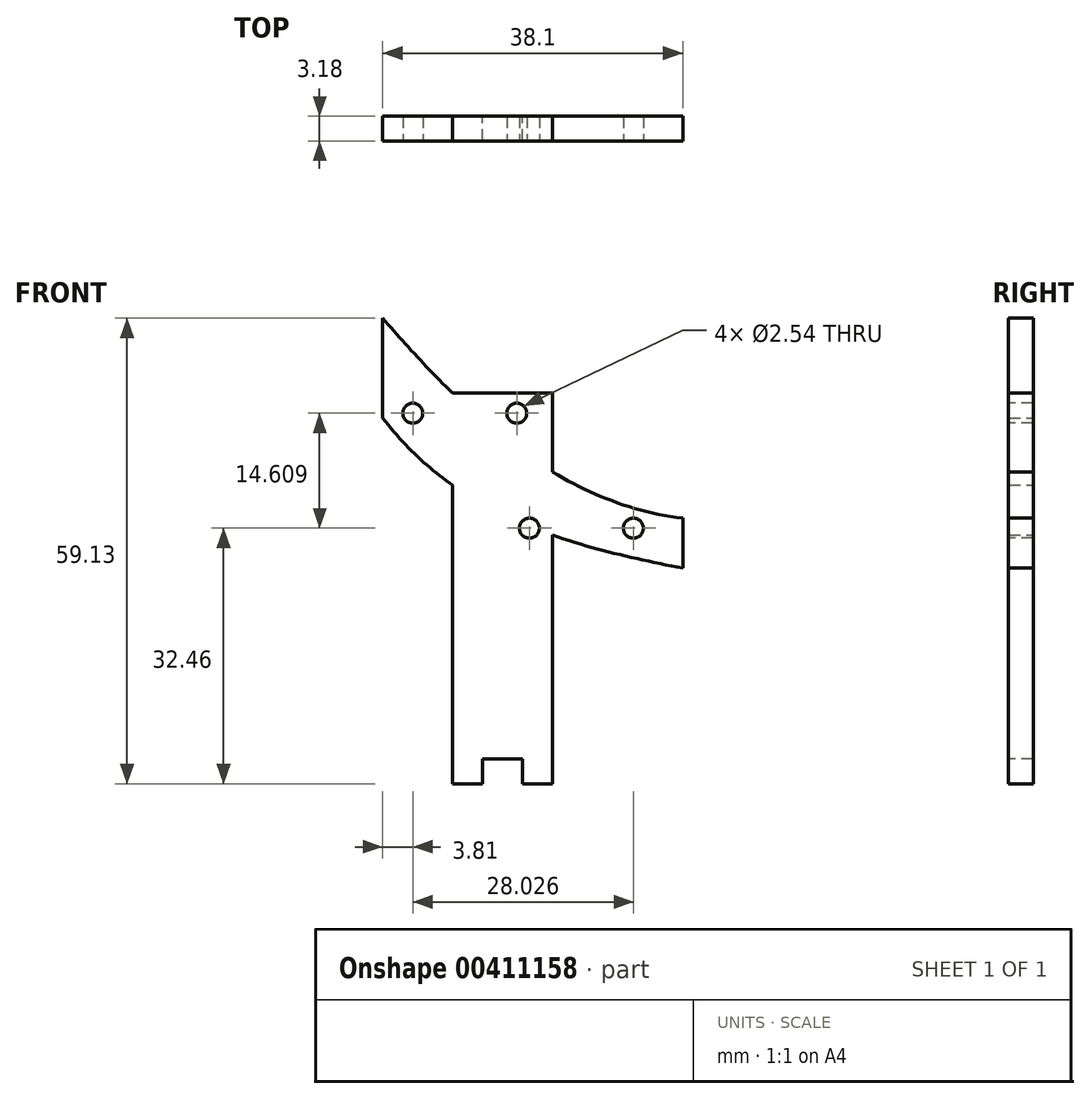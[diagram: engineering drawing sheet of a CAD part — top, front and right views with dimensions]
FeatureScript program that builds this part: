
annotation { "Feature Type Name" : "Feature", "Feature Type Description" : "" }
export const myFeature = defineFeature(function(context is Context, id is Id, definition is map)
    precondition{}
    {
        {
            var Q0;
            Q0=qCreatedBy(makeId("Front.planeOp"),FACE);
            var sketch = newSketch(context, id + "F0", { "sketchPlane" : qUnion([Q0])});
            skLineSegment(sketch, "E0", {"start": v(0, 0) * mm, "end": v(0, 6.35) * mm});
            skLineSegment(sketch, "E1", {"start": v(-38.1, 31.75) * mm, "end": v(-38.1, 19.05) * mm});
            skFitSpline(sketch, "E2", {"points": [v(-38.1, 19.05) * mm, v(0, 0) * mm], "startDerivative": vector(29.18, -37.97) * mm, "endDerivative": vector(42.34, -8.3) * mm});
            skFitSpline(sketch, "E3", {"points": [v(-38.1, 31.75) * mm, v(0, 6.35) * mm], "startDerivative": vector(26.62, -30.7) * mm, "endDerivative": vector(50, -5.86) * mm});
            skSolve(sketch);
        }
        {
            var Q0;
            Q0 = qSketchRegion(id + "F0", true);
            extrude(context, id + "F1", {"entities" : qUnion([Q0]), "depth" : 3.17 * mm});
        }
        {
            var Q0;
            Q0=makeQuery(id+"F1.opExtrude","CAP_FACE",FACE,{"disambiguationData":[OSD([sQuery(id+"F0.wireOp",EDGE,"E0"),sQuery(id+"F0.wireOp",EDGE,"E1"),sQuery(id+"F0.wireOp",EDGE,"E2"),sQuery(id+"F0.wireOp",EDGE,"E3")])],"isStart":false});
            var sketch = newSketch(context, id + "F2", { "sketchPlane" : qUnion([Q0])});
            skLineSegment(sketch, "E4.bottom", {"start": v(-29.22, 12.23) * mm, "end": v(-16.52, 12.23) * mm});
            skLineSegment(sketch, "E4.top", {"start": v(-29.22, -27.38) * mm, "end": v(-16.52, -27.38) * mm});
            skLineSegment(sketch, "E4.left", {"start": v(-29.22, 12.23) * mm, "end": v(-29.22, -27.38) * mm});
            skLineSegment(sketch, "E4.right", {"start": v(-16.52, 12.23) * mm, "end": v(-16.52, -27.38) * mm});
            skSolve(sketch);
        }
        {
            var Q0;
            Q0 = qSketchRegion(id + "F2", true);
            var Q1;
            Q1=makeQuery(id+"F1.opExtrude","CAP_FACE",FACE,{"disambiguationData":[OSD([sQuery(id+"F0.wireOp",EDGE,"E0"),sQuery(id+"F0.wireOp",EDGE,"E1"),sQuery(id+"F0.wireOp",EDGE,"E2"),sQuery(id+"F0.wireOp",EDGE,"E3")])],"isStart":true});
            extrude(context, id + "F3", {"entities" : qUnion([Q0]), "operationType" : NewBodyOperationType.ADD, "endBound" : BoundingType.UP_TO_SURFACE, "oppositeDirection" : true, "endBoundEntityFace" : qUnion([Q1]), "depth" : 25.4 * mm});
        }
        {
            var Q0;
            Q0=makeQuery(id+"F3.boolean.opBoolean","MERGE",FACE,{"derivedFrom":[makeQuery(id+"F1.opExtrude","CAP_FACE",FACE,{"disambiguationData":[OSD([sQuery(id+"F0.wireOp",EDGE,"E0"),sQuery(id+"F0.wireOp",EDGE,"E1"),sQuery(id+"F0.wireOp",EDGE,"E2"),sQuery(id+"F0.wireOp",EDGE,"E3")])],"isStart":false}),makeQuery(id+"F3.opExtrude","CAP_FACE",FACE,{"disambiguationData":[OSD([sQuery(id+"F2.wireOp",EDGE,"E4.bottom"),sQuery(id+"F2.wireOp",EDGE,"E4.top"),sQuery(id+"F2.wireOp",EDGE,"E4.left"),sQuery(id+"F2.wireOp",EDGE,"E4.right")])],"isStart":true})]});
            var sketch = newSketch(context, id + "F4", { "sketchPlane" : qUnion([Q0])});
            skLineSegment(sketch, "E5.bottom", {"start": v(-29.22, 10.54) * mm, "end": v(-16.52, 10.54) * mm});
            skLineSegment(sketch, "E5.top", {"start": v(-29.22, 22.23) * mm, "end": v(-16.52, 22.23) * mm});
            skLineSegment(sketch, "E5.left", {"start": v(-29.22, 10.54) * mm, "end": v(-29.22, 22.23) * mm});
            skLineSegment(sketch, "E5.right", {"start": v(-16.52, 10.54) * mm, "end": v(-16.52, 22.23) * mm});
            skSolve(sketch);
        }
        {
            var Q0;
            {var subQ0=sQuery(id+"F4.wireOp",EDGE,"E5.top");Q0=makeQuery(id+"F4.imprint","IMPRINT",FACE,{"disambiguationData":[TD([[makeQuery(id+"F4.imprint","IMPRINT",EDGE,{"derivedFrom":subQ0}),-1.0]])]});}
            var Q1;
            {var subQ0=sQuery(id+"F0.wireOp",EDGE,"E3");var subQ1=sQuery(id+"F0.wireOp",EDGE,"E2");var subQ2=sQuery(id+"F0.wireOp",EDGE,"E1");var subQ3=sQuery(id+"F0.wireOp",EDGE,"E0");Q1=makeQuery(id+"F3.boolean.opBoolean","MERGE",FACE,{"derivedFrom":[makeQuery(id+"F1.opExtrude","CAP_FACE",FACE,{"disambiguationData":[OSD([subQ3,subQ2,subQ1,subQ0])],"isStart":true}),makeQuery(id+"F3.opExtrude","CAP_FACE",FACE,{"disambiguationData":[OSD([subQ3,subQ2,subQ1,subQ0])],"isStart":false})]});}
            extrude(context, id + "F5", {"entities" : qUnion([Q0]), "operationType" : NewBodyOperationType.ADD, "endBound" : BoundingType.UP_TO_SURFACE, "oppositeDirection" : true, "endBoundEntityFace" : qUnion([Q1]), "depth" : 25.4 * mm});
        }
        {
            var Q0;
            {var subQ0=sQuery(id+"F0.wireOp",EDGE,"E3");Q0=makeQuery(id+"F5.boolean.opBoolean","MERGE",FACE,{"derivedFrom":[makeQuery(id+"F3.boolean.opBoolean","MERGE",FACE,{"derivedFrom":[makeQuery(id+"F1.opExtrude","CAP_FACE",FACE,{"disambiguationData":[OSD([sQuery(id+"F0.wireOp",EDGE,"E0"),sQuery(id+"F0.wireOp",EDGE,"E1"),sQuery(id+"F0.wireOp",EDGE,"E2"),subQ0])],"isStart":false}),makeQuery(id+"F3.opExtrude","CAP_FACE",FACE,{"disambiguationData":[OSD([sQuery(id+"F2.wireOp",EDGE,"E4.bottom"),sQuery(id+"F2.wireOp",EDGE,"E4.top"),sQuery(id+"F2.wireOp",EDGE,"E4.left"),sQuery(id+"F2.wireOp",EDGE,"E4.right")])],"isStart":true})]}),makeQuery(id+"F5.opExtrude","CAP_FACE",FACE,{"disambiguationData":[OSD([subQ0,sQuery(id+"F4.wireOp",EDGE,"E5.top"),sQuery(id+"F4.wireOp",EDGE,"E5.right")])],"isStart":true})]});}
            var sketch = newSketch(context, id + "F6", { "sketchPlane" : qUnion([Q0])});
            skCircle(sketch, "E6", {"center": v(-34.3, 19.69) * mm, "radius": 1.27 * mm});
            skCircle(sketch, "E7", {"center": v(-21.08, 19.69) * mm, "radius": 1.27 * mm});
            skSolve(sketch);
        }
        {
            var Q0;
            Q0 = qSketchRegion(id + "F6", true);
            extrude(context, id + "F7", {"entities" : qUnion([Q0]), "operationType" : NewBodyOperationType.REMOVE, "endBound" : BoundingType.THROUGH_ALL, "oppositeDirection" : true, "depth" : 25.4 * mm});
        }
        {
            var Q0;
            {var subQ0=sQuery(id+"F0.wireOp",EDGE,"E3");Q0=makeQuery(id+"F5.boolean.opBoolean","MERGE",FACE,{"derivedFrom":[makeQuery(id+"F3.boolean.opBoolean","MERGE",FACE,{"derivedFrom":[makeQuery(id+"F1.opExtrude","CAP_FACE",FACE,{"disambiguationData":[OSD([sQuery(id+"F0.wireOp",EDGE,"E0"),sQuery(id+"F0.wireOp",EDGE,"E1"),sQuery(id+"F0.wireOp",EDGE,"E2"),subQ0])],"isStart":false}),makeQuery(id+"F3.opExtrude","CAP_FACE",FACE,{"disambiguationData":[OSD([sQuery(id+"F2.wireOp",EDGE,"E4.bottom"),sQuery(id+"F2.wireOp",EDGE,"E4.top"),sQuery(id+"F2.wireOp",EDGE,"E4.left"),sQuery(id+"F2.wireOp",EDGE,"E4.right")])],"isStart":true})]}),makeQuery(id+"F5.opExtrude","CAP_FACE",FACE,{"disambiguationData":[OSD([subQ0,sQuery(id+"F4.wireOp",EDGE,"E5.top"),sQuery(id+"F4.wireOp",EDGE,"E5.right")])],"isStart":true})]});}
            var sketch = newSketch(context, id + "F8", { "sketchPlane" : qUnion([Q0])});
            skCircle(sketch, "E8", {"center": v(-6.26, 5.08) * mm, "radius": 1.27 * mm});
            skCircle(sketch, "E9", {"center": v(-19.47, 5.08) * mm, "radius": 1.27 * mm});
            skSolve(sketch);
        }
        {
            var Q0;
            Q0=makeQuery(id+"F8.imprint","IMPRINT",FACE,{"disambiguationData":[TD([[makeQuery(id+"F8.imprint","IMPRINT",EDGE,{"derivedFrom":sQuery(id+"F8.wireOp",EDGE,"E9")}),1.0]])]});
            var Q1;
            Q1=makeQuery(id+"F8.imprint","IMPRINT",FACE,{"disambiguationData":[TD([[makeQuery(id+"F8.imprint","IMPRINT",EDGE,{"derivedFrom":sQuery(id+"F8.wireOp",EDGE,"E8")}),1.0]])]});
            extrude(context, id + "F9", {"entities" : qUnion([Q0, Q1]), "operationType" : NewBodyOperationType.REMOVE, "endBound" : BoundingType.THROUGH_ALL, "oppositeDirection" : true, "depth" : 25.4 * mm});
        }
        {
            var Q0;
            {var subQ0=sQuery(id+"F0.wireOp",EDGE,"E3");Q0=makeQuery(id+"F5.boolean.opBoolean","MERGE",FACE,{"derivedFrom":[makeQuery(id+"F3.boolean.opBoolean","MERGE",FACE,{"derivedFrom":[makeQuery(id+"F1.opExtrude","CAP_FACE",FACE,{"disambiguationData":[OSD([sQuery(id+"F0.wireOp",EDGE,"E0"),sQuery(id+"F0.wireOp",EDGE,"E1"),sQuery(id+"F0.wireOp",EDGE,"E2"),subQ0])],"isStart":false}),makeQuery(id+"F3.opExtrude","CAP_FACE",FACE,{"disambiguationData":[OSD([sQuery(id+"F2.wireOp",EDGE,"E4.bottom"),sQuery(id+"F2.wireOp",EDGE,"E4.top"),sQuery(id+"F2.wireOp",EDGE,"E4.left"),sQuery(id+"F2.wireOp",EDGE,"E4.right")])],"isStart":true})]}),makeQuery(id+"F5.opExtrude","CAP_FACE",FACE,{"disambiguationData":[OSD([subQ0,sQuery(id+"F4.wireOp",EDGE,"E5.top"),sQuery(id+"F4.wireOp",EDGE,"E5.right")])],"isStart":true})]});}
            var sketch = newSketch(context, id + "F10", { "sketchPlane" : qUnion([Q0])});
            skLineSegment(sketch, "E10.bottom", {"start": v(-25.41, -24.2) * mm, "end": v(-20.33, -24.2) * mm});
            skLineSegment(sketch, "E10.top", {"start": v(-25.41, -30.56) * mm, "end": v(-20.33, -30.56) * mm});
            skLineSegment(sketch, "E10.left", {"start": v(-25.41, -24.2) * mm, "end": v(-25.41, -30.56) * mm});
            skLineSegment(sketch, "E10.right", {"start": v(-20.33, -24.2) * mm, "end": v(-20.33, -30.56) * mm});
            skPoint(sketch, "E10.middle", {"position": v(-22.87, -27.38) * mm});
            skSolve(sketch);
        }
        {
            var Q0;
            Q0 = qSketchRegion(id + "F10", true);
            extrude(context, id + "F11", {"entities" : qUnion([Q0]), "operationType" : NewBodyOperationType.REMOVE, "oppositeDirection" : true, "depth" : 25.4 * mm});
        }
    });
